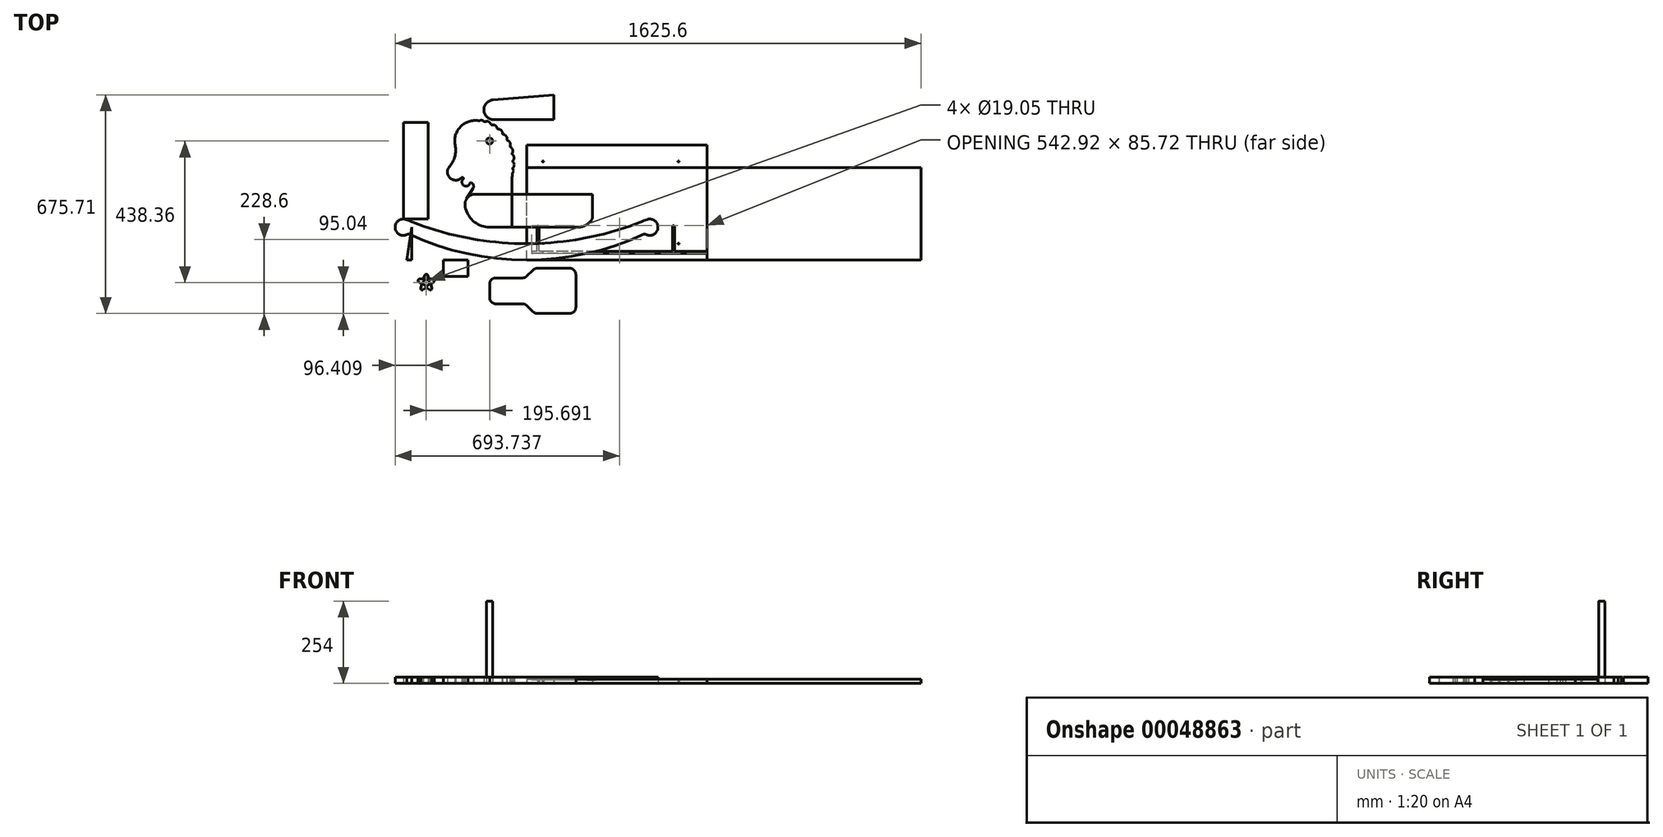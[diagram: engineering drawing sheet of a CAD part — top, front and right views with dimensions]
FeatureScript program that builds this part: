
annotation { "Feature Type Name" : "Feature", "Feature Type Description" : "" }
export const myFeature = defineFeature(function(context is Context, id is Id, definition is map)
    precondition{}
    {
        {
            var Q0;
            Q0=qCreatedBy(makeId("Top.planeOp"),FACE);
            var sketch = newSketch(context, id + "F23", { "sketchPlane" : qUnion([Q0])});
            skArc(sketch, "E0", {"start": v(368.4, 79.55) * mm, "mid": v(406.35, 100.02) * mm, "end": v(371.23, 125.05) * mm});
            skArc(sketch, "E1", {"start": v(-371.23, 125.05) * mm, "mid": v(-406.35, 100.02) * mm, "end": v(-368.4, 79.55) * mm});
            skArc(sketch, "E2", {"start": v(-362.58, 79.8) * mm, "mid": v(0, 0) * mm, "end": v(362.58, 79.8) * mm});
            skArc(sketch, "E3", {"start": v(-371.23, 125.05) * mm, "mid": v(-305.78, 100.52) * mm, "end": v(-238.73, 80.79) * mm});
            skPoint(sketch, "E4.visualSharp", {"position": v(365.76, 81.28) * mm});
            skArc(sketch, "E4.filletArc", {"start": v(368.4, 79.55) * mm, "mid": v(365.52, 80.38) * mm, "end": v(362.58, 79.8) * mm});
            skPoint(sketch, "E5.visualSharp", {"position": v(-365.76, 81.28) * mm});
            skArc(sketch, "E5.filletArc", {"start": v(-362.58, 79.8) * mm, "mid": v(-365.52, 80.38) * mm, "end": v(-368.4, 79.55) * mm});
            skLineSegment(sketch, "E6", {"start": v(-238.73, 80.79) * mm, "end": v(-151.67, 62.8) * mm});
            skArc(sketch, "E7.trimOffspring", {"start": v(-151.67, 62.8) * mm, "mid": v(0, 50.8) * mm, "end": v(151.67, 62.8) * mm});
            skLineSegment(sketch, "E8", {"start": v(238.73, 80.79) * mm, "end": v(151.67, 62.8) * mm});
            skArc(sketch, "E9.trimOffspring", {"start": v(238.73, 80.79) * mm, "mid": v(305.78, 100.52) * mm, "end": v(371.23, 125.05) * mm});
            skSolve(sketch);
        }
        {
            var Q0;
            Q0 = qSketchRegion(id + "F23", true);
            extrude(context, id + "F0", {"entities" : qUnion([Q0]), "depth" : 19.05 * mm});
        }
        {
            var Q0;
            Q0=qCreatedBy(makeId("Top.planeOp"),FACE);
            var sketch = newSketch(context, id + "F1", { "sketchPlane" : qUnion([Q0])});
            skLineSegment(sketch, "E10.bottom", {"start": v(-190.5, 203.2) * mm, "end": v(203.2, 203.2) * mm, "construction": true});
            skLineSegment(sketch, "E10.top", {"start": v(-190.5, 101.6) * mm, "end": v(203.2, 101.6) * mm, "construction": true});
            skLineSegment(sketch, "E10.left", {"start": v(-190.5, 203.2) * mm, "end": v(-190.5, 101.6) * mm, "construction": true});
            skLineSegment(sketch, "E10.right", {"start": v(203.2, 203.2) * mm, "end": v(203.2, 101.6) * mm, "construction": true});
            skArc(sketch, "E11", {"start": v(-165.1, 203.2) * mm, "mid": v(-185.7, 188.88) * mm, "end": v(-189.47, 164.07) * mm});
            skLineSegment(sketch, "E12", {"start": v(-189.47, 164.07) * mm, "end": v(-188.03, 158.55) * mm});
            skArc(sketch, "E13", {"start": v(-188.03, 158.55) * mm, "mid": v(-160.88, 117.5) * mm, "end": v(-114.3, 101.6) * mm});
            skArc(sketch, "E14", {"start": v(159.2, 101.6) * mm, "mid": v(183.79, 107.94) * mm, "end": v(202.23, 125.39) * mm});
            skLineSegment(sketch, "E15", {"start": v(-165.1, 203.2) * mm, "end": v(203.2, 203.2) * mm});
            skLineSegment(sketch, "E16", {"start": v(203.2, 203.2) * mm, "end": v(203.2, 128.76) * mm});
            skLineSegment(sketch, "E17", {"start": v(159.2, 101.6) * mm, "end": v(-114.3, 101.6) * mm});
            skPoint(sketch, "E18.visualSharp", {"position": v(203.2, 127) * mm});
            skArc(sketch, "E18.filletArc", {"start": v(202.23, 125.39) * mm, "mid": v(202.95, 127) * mm, "end": v(203.2, 128.76) * mm});
            skArc(sketch, "E19", {"start": v(-165.57, 221.2) * mm, "mid": v(-164.08, 231.17) * mm, "end": v(-170.33, 239.1) * mm});
            skArc(sketch, "E20", {"start": v(-196.2, 250.12) * mm, "mid": v(-193.66, 230.45) * mm, "end": v(-175.03, 237.24) * mm});
            skArc(sketch, "E21", {"start": v(-238.28, 289.15) * mm, "mid": v(-236.44, 253.68) * mm, "end": v(-200.95, 254.7) * mm});
            skArc(sketch, "E22", {"start": v(-146.05, 430.52) * mm, "mid": v(-203.79, 413.06) * mm, "end": v(-220.89, 355.22) * mm});
            skLineSegment(sketch, "E23", {"start": v(-185.7, 188.88) * mm, "end": v(-165.57, 221.2) * mm});
            skArc(sketch, "E24", {"start": v(-238.28, 289.15) * mm, "mid": v(-221.76, 320.12) * mm, "end": v(-220.89, 355.22) * mm});
            skArc(sketch, "E25", {"start": v(-44.45, 306.08) * mm, "mid": v(-73.08, 386.4) * mm, "end": v(-146.05, 430.52) * mm, "construction": true});
            skLineSegment(sketch, "E26", {"start": v(-44.45, 305.7) * mm, "end": v(-44.45, 203.2) * mm, "construction": true});
            skArc(sketch, "E27", {"start": v(-196.2, 250.12) * mm, "mid": v(-196.28, 254.8) * mm, "end": v(-200.95, 254.7) * mm});
            skLineSegment(sketch, "E28", {"start": v(-220.72, 382.14) * mm, "end": v(-244, 277.9) * mm, "construction": true});
            skLineSegment(sketch, "E29", {"start": v(-44.45, 203.2) * mm, "end": v(-44.45, 101.6) * mm});
            skLineSegment(sketch, "E30", {"start": v(-219.22, 272.35) * mm, "end": v(-187.06, 241.3) * mm, "construction": true});
            skPoint(sketch, "E31.visualSharp", {"position": v(-174.4, 240.46) * mm});
            skArc(sketch, "E31.filletArc", {"start": v(-170.33, 239.1) * mm, "mid": v(-173.11, 239.26) * mm, "end": v(-175.03, 237.24) * mm});
            skArc(sketch, "E32", {"start": v(-130.35, 426.25) * mm, "mid": v(-137.13, 432.31) * mm, "end": v(-146.05, 430.52) * mm});
            skArc(sketch, "E33", {"start": v(-109.75, 417.09) * mm, "mid": v(-117.27, 427.93) * mm, "end": v(-130.35, 426.25) * mm});
            skArc(sketch, "E34", {"start": v(-91.1, 404.43) * mm, "mid": v(-96.58, 416.43) * mm, "end": v(-109.75, 417.09) * mm});
            skArc(sketch, "E35", {"start": v(-74.97, 388.67) * mm, "mid": v(-78.24, 401.45) * mm, "end": v(-91.1, 404.43) * mm});
            skArc(sketch, "E36", {"start": v(-61.89, 370.3) * mm, "mid": v(-62.85, 383.47) * mm, "end": v(-74.97, 388.67) * mm});
            skArc(sketch, "E37", {"start": v(-52.26, 349.92) * mm, "mid": v(-50.88, 363.04) * mm, "end": v(-61.89, 370.3) * mm});
            skArc(sketch, "E38", {"start": v(-46.38, 328.16) * mm, "mid": v(-42.7, 340.83) * mm, "end": v(-52.26, 349.92) * mm});
            skArc(sketch, "E39", {"start": v(-44.45, 305.7) * mm, "mid": v(-38.6, 317.51) * mm, "end": v(-46.38, 328.16) * mm});
            skArc(sketch, "E40", {"start": v(-44.45, 283.7) * mm, "mid": v(-38.1, 294.7) * mm, "end": v(-44.45, 305.7) * mm});
            skArc(sketch, "E41", {"start": v(-44.45, 267.83) * mm, "mid": v(-40.64, 275.77) * mm, "end": v(-44.45, 283.7) * mm});
            skArc(sketch, "E42", {"start": v(-44.45, 259.4) * mm, "mid": v(-43.18, 263.62) * mm, "end": v(-44.45, 267.83) * mm});
            skLineSegment(sketch, "E43", {"start": v(-44.45, 259.4) * mm, "end": v(-44.45, 203.2) * mm});
            skCircle(sketch, "E44", {"center": v(-114.3, 368.3) * mm, "radius": 9.53 * mm});
            skSolve(sketch);
        }
        {
            var Q0;
            Q0=qCreatedBy(makeId("Top.planeOp"),FACE);
            var sketch = newSketch(context, id + "F2", { "sketchPlane" : qUnion([Q0])});
            skLineSegment(sketch, "E45.bottom", {"start": v(-95.25, -55.25) * mm, "end": v(-12.34, -55.25) * mm});
            skLineSegment(sketch, "E45.top", {"start": v(-95.25, -135.26) * mm, "end": v(-12.34, -135.26) * mm});
            skLineSegment(sketch, "E45.left", {"start": v(-114.3, -74.3) * mm, "end": v(-114.3, -116.2) * mm});
            skLineSegment(sketch, "E46.bottom", {"start": v(33.3, -25.4) * mm, "end": v(133.35, -25.4) * mm});
            skLineSegment(sketch, "E46.top", {"start": v(33.3, -165.1) * mm, "end": v(133.35, -165.1) * mm});
            skLineSegment(sketch, "E46.right", {"start": v(152.4, -44.45) * mm, "end": v(152.4, -146.05) * mm});
            skLineSegment(sketch, "E47", {"start": v(1.13, -49.67) * mm, "end": v(19.82, -30.98) * mm});
            skLineSegment(sketch, "E48", {"start": v(1.13, -140.83) * mm, "end": v(19.82, -159.52) * mm});
            skPoint(sketch, "E49.visualSharp", {"position": v(-4.45, -55.25) * mm});
            skArc(sketch, "E49.filletArc", {"start": v(-12.34, -55.25) * mm, "mid": v(-5.05, -53.8) * mm, "end": v(1.13, -49.67) * mm});
            skPoint(sketch, "E50.visualSharp", {"position": v(25.4, -25.4) * mm});
            skArc(sketch, "E50.filletArc", {"start": v(33.3, -25.4) * mm, "mid": v(26, -26.85) * mm, "end": v(19.82, -30.98) * mm});
            skPoint(sketch, "E51.visualSharp", {"position": v(-4.44, -135.26) * mm});
            skArc(sketch, "E51.filletArc", {"start": v(1.13, -140.83) * mm, "mid": v(-5.05, -136.7) * mm, "end": v(-12.34, -135.26) * mm});
            skPoint(sketch, "E52.visualSharp", {"position": v(25.4, -165.1) * mm});
            skArc(sketch, "E52.filletArc", {"start": v(19.82, -159.52) * mm, "mid": v(26, -163.65) * mm, "end": v(33.3, -165.1) * mm});
            skLineSegment(sketch, "E53", {"start": v(-114.3, -95.25) * mm, "end": v(152.4, -95.25) * mm, "construction": true});
            skPoint(sketch, "E54.visualSharp", {"position": v(-114.3, -55.25) * mm});
            skArc(sketch, "E54.filletArc", {"start": v(-95.25, -55.24) * mm, "mid": v(-108.72, -60.82) * mm, "end": v(-114.3, -74.3) * mm});
            skPoint(sketch, "E55.visualSharp", {"position": v(-114.3, -135.25) * mm});
            skArc(sketch, "E55.filletArc", {"start": v(-114.3, -116.2) * mm, "mid": v(-108.72, -129.68) * mm, "end": v(-95.25, -135.26) * mm});
            skPoint(sketch, "E56.visualSharp", {"position": v(152.4, -165.1) * mm});
            skArc(sketch, "E56.filletArc", {"start": v(133.35, -165.1) * mm, "mid": v(146.82, -159.52) * mm, "end": v(152.4, -146.05) * mm});
            skPoint(sketch, "E57.visualSharp", {"position": v(152.4, -25.4) * mm});
            skArc(sketch, "E57.filletArc", {"start": v(152.4, -44.45) * mm, "mid": v(146.82, -30.98) * mm, "end": v(133.35, -25.4) * mm});
            skSolve(sketch);
        }
        {
            var Q0;
            Q0=qCreatedBy(makeId("Top.planeOp"),FACE);
            var sketch = newSketch(context, id + "F3", { "sketchPlane" : qUnion([Q0])});
            skLineSegment(sketch, "E58.bottom", {"start": v(-381, 425.45) * mm, "end": v(-304.8, 425.45) * mm});
            skLineSegment(sketch, "E58.top", {"start": v(-381, 127) * mm, "end": v(-304.8, 127) * mm});
            skLineSegment(sketch, "E58.left", {"start": v(-381, 425.45) * mm, "end": v(-381, 127) * mm});
            skLineSegment(sketch, "E58.right", {"start": v(-304.8, 425.45) * mm, "end": v(-304.8, 127) * mm});
            skSolve(sketch);
        }
        {
            var Q0;
            Q0=qCreatedBy(makeId("Top.planeOp"),FACE);
            var sketch = newSketch(context, id + "F4", { "sketchPlane" : qUnion([Q0])});
            skLineSegment(sketch, "E59", {"start": v(-370.84, 0) * mm, "end": v(-355.6, 101.6) * mm});
            skLineSegment(sketch, "E60", {"start": v(-355.6, 101.6) * mm, "end": v(-355.6, 0) * mm});
            skLineSegment(sketch, "E61", {"start": v(-355.6, 0) * mm, "end": v(-370.84, 0) * mm});
            skCircle(sketch, "E62.cCircle", {"center": v(-310, -70.06) * mm, "radius": 37.8 * mm, "construction": true});
            skLineSegment(sketch, "E62.0", {"start": v(-332.21, -100.64) * mm, "end": v(-345.95, -58.38) * mm, "construction": true});
            skLineSegment(sketch, "E62.1", {"start": v(-345.95, -58.38) * mm, "end": v(-310, -32.25) * mm, "construction": true});
            skLineSegment(sketch, "E62.2", {"start": v(-310, -32.25) * mm, "end": v(-274.04, -58.38) * mm, "construction": true});
            skLineSegment(sketch, "E62.3", {"start": v(-274.04, -58.38) * mm, "end": v(-287.77, -100.64) * mm, "construction": true});
            skLineSegment(sketch, "E62.4", {"start": v(-287.77, -100.64) * mm, "end": v(-332.21, -100.64) * mm, "construction": true});
            skLineSegment(sketch, "E63", {"start": v(-330.31, -58.38) * mm, "end": v(-320.88, -58.38) * mm});
            skLineSegment(sketch, "E64", {"start": v(-319.56, -91.45) * mm, "end": v(-311.93, -85.91) * mm});
            skLineSegment(sketch, "E65", {"start": v(-300.42, -91.45) * mm, "end": v(-308.05, -85.91) * mm});
            skLineSegment(sketch, "E66", {"start": v(-314.82, -47.12) * mm, "end": v(-317.74, -56.1) * mm});
            skLineSegment(sketch, "E67", {"start": v(-305.16, -47.12) * mm, "end": v(-302.24, -56.1) * mm});
            skLineSegment(sketch, "E68.trimOffspring", {"start": v(-295.52, -76.8) * mm, "end": v(-292.6, -85.78) * mm});
            skLineSegment(sketch, "E69.trimOffspring", {"start": v(-299.1, -58.38) * mm, "end": v(-289.67, -58.38) * mm});
            skLineSegment(sketch, "E70.trimOffspring", {"start": v(-324.47, -76.8) * mm, "end": v(-327.38, -85.78) * mm});
            skLineSegment(sketch, "E71.trimOffspring", {"start": v(-325.67, -73.11) * mm, "end": v(-333.3, -67.57) * mm});
            skLineSegment(sketch, "E72.trimOffspring", {"start": v(-294.32, -73.11) * mm, "end": v(-286.69, -67.57) * mm});
            skPoint(sketch, "E73.visualSharp", {"position": v(-301.5, -58.38) * mm});
            skArc(sketch, "E73.filletArc", {"start": v(-302.24, -56.1) * mm, "mid": v(-301.05, -57.75) * mm, "end": v(-299.1, -58.38) * mm});
            skPoint(sketch, "E74.visualSharp", {"position": v(-318.48, -58.38) * mm});
            skArc(sketch, "E74.filletArc", {"start": v(-320.88, -58.38) * mm, "mid": v(-318.94, -57.75) * mm, "end": v(-317.74, -56.1) * mm});
            skPoint(sketch, "E75.visualSharp", {"position": v(-323.72, -74.52) * mm});
            skArc(sketch, "E75.filletArc", {"start": v(-324.47, -76.8) * mm, "mid": v(-324.47, -74.76) * mm, "end": v(-325.67, -73.11) * mm});
            skPoint(sketch, "E76.visualSharp", {"position": v(-310, -84.5) * mm});
            skArc(sketch, "E76.filletArc", {"start": v(-308.05, -85.91) * mm, "mid": v(-310, -85.28) * mm, "end": v(-311.93, -85.91) * mm});
            skPoint(sketch, "E77.visualSharp", {"position": v(-296.26, -74.52) * mm});
            skArc(sketch, "E77.filletArc", {"start": v(-294.32, -73.11) * mm, "mid": v(-295.52, -74.76) * mm, "end": v(-295.52, -76.8) * mm});
            skCircle(sketch, "E78", {"center": v(-310, -70.06) * mm, "radius": 9.53 * mm});
            skPoint(sketch, "E79.visualSharp", {"position": v(-310, -32.25) * mm});
            skArc(sketch, "E79.filletArc", {"start": v(-305.16, -47.12) * mm, "mid": v(-310, -43.61) * mm, "end": v(-314.82, -47.12) * mm});
            skPoint(sketch, "E80.visualSharp", {"position": v(-274.04, -58.38) * mm});
            skArc(sketch, "E80.filletArc", {"start": v(-286.69, -67.57) * mm, "mid": v(-284.84, -61.89) * mm, "end": v(-289.67, -58.38) * mm});
            skPoint(sketch, "E81.visualSharp", {"position": v(-345.95, -58.38) * mm});
            skArc(sketch, "E81.filletArc", {"start": v(-330.31, -58.38) * mm, "mid": v(-335.14, -61.89) * mm, "end": v(-333.3, -67.57) * mm});
            skPoint(sketch, "E82.visualSharp", {"position": v(-332.21, -100.64) * mm});
            skArc(sketch, "E82.filletArc", {"start": v(-327.38, -85.78) * mm, "mid": v(-325.54, -91.45) * mm, "end": v(-319.56, -91.45) * mm});
            skPoint(sketch, "E83.visualSharp", {"position": v(-287.77, -100.64) * mm});
            skArc(sketch, "E83.filletArc", {"start": v(-300.42, -91.45) * mm, "mid": v(-294.45, -91.45) * mm, "end": v(-292.6, -85.78) * mm});
            skSolve(sketch);
        }
        {
            var Q0;
            Q0=qCreatedBy(makeId("Top.planeOp"),FACE);
            var sketch = newSketch(context, id + "F5", { "sketchPlane" : qUnion([Q0])});
            skLineSegment(sketch, "E84.bottom", {"start": v(83.86, 510.61) * mm, "end": v(-104.04, 495.27) * mm});
            skLineSegment(sketch, "E84.top", {"start": v(83.86, 434.41) * mm, "end": v(-101.56, 434.41) * mm});
            skLineSegment(sketch, "E84.left", {"start": v(83.86, 510.61) * mm, "end": v(83.86, 434.41) * mm});
            skArc(sketch, "E85", {"start": v(-104.04, 495.27) * mm, "mid": v(-132.02, 463.65) * mm, "end": v(-101.56, 434.41) * mm});
            skSolve(sketch);
        }
        {
            var Q0;
            Q0=makeQuery(id+"F3.imprint","IMPRINT",FACE,{"disambiguationData":[TD([[makeQuery(id+"F3.imprint","IMPRINT",EDGE,{"derivedFrom":sQuery(id+"F3.wireOp",EDGE,"E58.bottom")}),-1.0]])]});
            extrude(context, id + "F6", {"entities" : qUnion([Q0]), "depth" : 19.05 * mm});
        }
        {
            var Q0;
            Q0=makeQuery(id+"F1.imprint","IMPRINT",FACE,{"disambiguationData":[TD([[makeQuery(id+"F1.imprint","IMPRINT",EDGE,{"derivedFrom":sQuery(id+"F1.wireOp",EDGE,"E11")}),1.0]])]});
            var Q1;
            {var subQ1=sQuery(id+"F1.wireOp",EDGE,"E14");Q1=makeQuery(id+"F1.imprint","IMPRINT",FACE,{"disambiguationData":[TD([[makeQuery(id+"F1.imprint","IMPRINT",EDGE,{"derivedFrom":subQ1}),1.0]])]});}
            extrude(context, id + "F7", {"entities" : qUnion([Q0, Q1]), "depth" : 19.05 * mm});
        }
        {
            var Q0;
            Q0=makeQuery(id+"F4.imprint","IMPRINT",FACE,{"disambiguationData":[TD([[makeQuery(id+"F4.imprint","IMPRINT",EDGE,{"derivedFrom":sQuery(id+"F4.wireOp",EDGE,"E59")}),-1.0]])]});
            extrude(context, id + "F8", {"entities" : qUnion([Q0]), "depth" : 19.05 * mm});
        }
        {
            var Q0;
            Q0=makeQuery(id+"F2.imprint","IMPRINT",FACE,{"disambiguationData":[TD([[makeQuery(id+"F2.imprint","IMPRINT",EDGE,{"derivedFrom":sQuery(id+"F2.wireOp",EDGE,"E45.bottom")}),-1.0]])]});
            extrude(context, id + "F24", {"entities" : qUnion([Q0]), "depth" : 19.05 * mm});
        }
        {
            var Q0;
            Q0=makeQuery(id+"F5.imprint","IMPRINT",FACE,{"disambiguationData":[TD([[makeQuery(id+"F5.imprint","IMPRINT",EDGE,{"derivedFrom":sQuery(id+"F5.wireOp",EDGE,"E84.bottom")}),1.0]])]});
            extrude(context, id + "F9", {"entities" : qUnion([Q0]), "depth" : 19.05 * mm});
        }
        {
            var Q0;
            {var subQ1=sQuery(id+"F1.wireOp",EDGE,"E12");Q0=makeQuery(id+"F1.imprint","IMPRINT",FACE,{"disambiguationData":[TD([[makeQuery(id+"F1.imprint","IMPRINT",EDGE,{"derivedFrom":subQ1}),1.0]])]});}
            var Q1;
            Q1=makeQuery(id+"F1.imprint","IMPRINT",FACE,{"disambiguationData":[TD([[makeQuery(id+"F1.imprint","IMPRINT",EDGE,{"derivedFrom":sQuery(id+"F1.wireOp",EDGE,"E19")}),-1.0]])]});
            extrude(context, id + "F10", {"entities" : qUnion([Q0, Q1]), "depth" : 19.05 * mm});
        }
        {
            var Q0;
            Q0=makeQuery(id+"F4.imprint","IMPRINT",FACE,{"disambiguationData":[TD([[makeQuery(id+"F4.imprint","IMPRINT",EDGE,{"derivedFrom":sQuery(id+"F4.wireOp",EDGE,"E63")}),-1.0]])]});
            extrude(context, id + "F11", {"entities" : qUnion([Q0]), "depth" : 19.05 * mm});
        }
        {
            var Q0;
            Q0=qCreatedBy(makeId("Top.planeOp"),FACE);
            var sketch = newSketch(context, id + "F12", { "sketchPlane" : qUnion([Q0])});
            skLineSegment(sketch, "E86.bottom", {"start": v(0, 0) * mm, "end": v(1219.2, 0) * mm});
            skLineSegment(sketch, "E86.top", {"start": v(0, 285.75) * mm, "end": v(1219.2, 285.75) * mm});
            skLineSegment(sketch, "E86.left", {"start": v(0, 0) * mm, "end": v(0, 285.75) * mm});
            skLineSegment(sketch, "E86.right", {"start": v(1219.2, 0) * mm, "end": v(1219.2, 285.75) * mm});
            skSolve(sketch);
        }
        {
            var Q0;
            Q0=makeQuery(id+"F12.imprint","IMPRINT",FACE,{"disambiguationData":[TD([[makeQuery(id+"F12.imprint","IMPRINT",EDGE,{"derivedFrom":sQuery(id+"F12.wireOp",EDGE,"E86.bottom")}),1.0]])]});
            extrude(context, id + "F13", {"entities" : qUnion([Q0]), "depth" : 12.7 * mm});
        }
        {
            var Q0;
            Q0=qCreatedBy(makeId("Top.planeOp"),FACE);
            var sketch = newSketch(context, id + "F14", { "sketchPlane" : qUnion([Q0])});
            skLineSegment(sketch, "E87.bottom", {"start": v(-256.73, 0) * mm, "end": v(-180.53, 0) * mm});
            skLineSegment(sketch, "E87.top", {"start": v(-256.73, -50.8) * mm, "end": v(-180.53, -50.8) * mm});
            skLineSegment(sketch, "E87.left", {"start": v(-256.73, 0) * mm, "end": v(-256.73, -50.8) * mm});
            skLineSegment(sketch, "E87.right", {"start": v(-180.53, 0) * mm, "end": v(-180.53, -50.8) * mm});
            skSolve(sketch);
        }
        {
            var Q0;
            Q0=makeQuery(id+"F14.imprint","IMPRINT",FACE,{"disambiguationData":[TD([[makeQuery(id+"F14.imprint","IMPRINT",EDGE,{"derivedFrom":sQuery(id+"F14.wireOp",EDGE,"E87.bottom")}),-1.0]])]});
            extrude(context, id + "F15", {"entities" : qUnion([Q0]), "depth" : 19.05 * mm});
        }
        {
            var Q0;
            Q0=qCreatedBy(makeId("Top.planeOp"),FACE);
            var sketch = newSketch(context, id + "F16", { "sketchPlane" : qUnion([Q0])});
            skLineSegment(sketch, "E88.bottom", {"start": v(0, 0) * mm, "end": v(558.8, 0) * mm});
            skLineSegment(sketch, "E88.top", {"start": v(0, 355.6) * mm, "end": v(558.8, 355.6) * mm});
            skLineSegment(sketch, "E88.left", {"start": v(0, 0) * mm, "end": v(0, 355.6) * mm});
            skLineSegment(sketch, "E88.right", {"start": v(558.8, 0) * mm, "end": v(558.8, 355.6) * mm});
            skPoint(sketch, "E89", {"position": v(50.8, 304.8) * mm});
            skPoint(sketch, "E90", {"position": v(50.8, 50.8) * mm});
            skPoint(sketch, "E91", {"position": v(469.9, 304.8) * mm});
            skPoint(sketch, "E92", {"position": v(469.9, 50.8) * mm});
            skLineSegment(sketch, "E93", {"start": v(50.8, 304.8) * mm, "end": v(50.8, 50.8) * mm, "construction": true});
            skLineSegment(sketch, "E94", {"start": v(50.8, 304.8) * mm, "end": v(469.9, 304.8) * mm, "construction": true});
            skLineSegment(sketch, "E95", {"start": v(469.9, 50.8) * mm, "end": v(469.9, 304.8) * mm, "construction": true});
            skLineSegment(sketch, "E96", {"start": v(469.9, 50.8) * mm, "end": v(50.8, 50.8) * mm, "construction": true});
            skCircle(sketch, "E97", {"center": v(50.8, 304.8) * mm, "radius": 1.59 * mm});
            skCircle(sketch, "E98", {"center": v(469.9, 304.8) * mm, "radius": 1.59 * mm});
            skCircle(sketch, "E99", {"center": v(469.9, 50.8) * mm, "radius": 1.59 * mm});
            skCircle(sketch, "E100", {"center": v(50.8, 50.8) * mm, "radius": 1.59 * mm});
            skLineSegment(sketch, "E101", {"start": v(50.8, 50.8) * mm, "end": v(50.8, 25.4) * mm, "construction": true});
            skLineSegment(sketch, "E102", {"start": v(469.9, 25.4) * mm, "end": v(469.9, 50.8) * mm, "construction": true});
            skLineSegment(sketch, "E103", {"start": v(50.8, 25.4) * mm, "end": v(469.9, 25.4) * mm, "construction": true});
            skCircle(sketch, "E104", {"center": v(50.8, 25.4) * mm, "radius": 1.59 * mm});
            skCircle(sketch, "E105", {"center": v(469.9, 25.4) * mm, "radius": 1.59 * mm});
            skCircle(sketch, "E106", {"center": v(36.51, 50.8) * mm, "radius": 1.59 * mm});
            skLineSegment(sketch, "E107", {"start": v(50.8, 50.8) * mm, "end": v(36.51, 50.8) * mm, "construction": true});
            skSolve(sketch);
        }
        {
            var Q0;
            Q0=makeQuery(id+"F16.imprint","IMPRINT",FACE,{"disambiguationData":[TD([[makeQuery(id+"F16.imprint","IMPRINT",EDGE,{"derivedFrom":sQuery(id+"F16.wireOp",EDGE,"E88.bottom")}),1.0]])]});
            extrude(context, id + "F17", {"entities" : qUnion([Q0]), "depth" : 12.7 * mm});
        }
        {
            var Q0;
            Q0=makeQuery(id+"F10.opExtrude","SWEPT_EDGE",EDGE,{"disambiguationData":[OSD([sQuery(id+"F1.wireOp",EDGE,"E22"),sQuery(id+"F1.wireOp",EDGE,"E32")])]});
            var Q1;
            Q1=makeQuery(id+"F10.opExtrude","SWEPT_EDGE",EDGE,{"disambiguationData":[OSD([sQuery(id+"F1.wireOp",EDGE,"E32"),sQuery(id+"F1.wireOp",EDGE,"E33")])]});
            var Q2;
            Q2=makeQuery(id+"F10.opExtrude","SWEPT_EDGE",EDGE,{"disambiguationData":[OSD([sQuery(id+"F1.wireOp",EDGE,"E33"),sQuery(id+"F1.wireOp",EDGE,"E34")])]});
            var Q3;
            Q3=makeQuery(id+"F10.opExtrude","SWEPT_EDGE",EDGE,{"disambiguationData":[OSD([sQuery(id+"F1.wireOp",EDGE,"E34"),sQuery(id+"F1.wireOp",EDGE,"E35")])]});
            var Q4;
            Q4=makeQuery(id+"F10.opExtrude","SWEPT_EDGE",EDGE,{"disambiguationData":[OSD([sQuery(id+"F1.wireOp",EDGE,"E35"),sQuery(id+"F1.wireOp",EDGE,"E36")])]});
            var Q5;
            Q5=makeQuery(id+"F10.opExtrude","SWEPT_EDGE",EDGE,{"disambiguationData":[OSD([sQuery(id+"F1.wireOp",EDGE,"E36"),sQuery(id+"F1.wireOp",EDGE,"E37")])]});
            var Q6;
            Q6=makeQuery(id+"F10.opExtrude","SWEPT_EDGE",EDGE,{"disambiguationData":[OSD([sQuery(id+"F1.wireOp",EDGE,"E37"),sQuery(id+"F1.wireOp",EDGE,"E38")])]});
            var Q7;
            Q7=makeQuery(id+"F10.opExtrude","SWEPT_EDGE",EDGE,{"disambiguationData":[OSD([sQuery(id+"F1.wireOp",EDGE,"E38"),sQuery(id+"F1.wireOp",EDGE,"E39")])]});
            var Q8;
            Q8=makeQuery(id+"F10.opExtrude","SWEPT_EDGE",EDGE,{"disambiguationData":[OSD([sQuery(id+"F1.wireOp",EDGE,"E39"),sQuery(id+"F1.wireOp",EDGE,"E40")])]});
            var Q9;
            Q9=makeQuery(id+"F10.opExtrude","SWEPT_EDGE",EDGE,{"disambiguationData":[OSD([sQuery(id+"F1.wireOp",EDGE,"E40"),sQuery(id+"F1.wireOp",EDGE,"E41")])]});
            var Q10;
            Q10=makeQuery(id+"F10.opExtrude","SWEPT_EDGE",EDGE,{"disambiguationData":[OSD([sQuery(id+"F1.wireOp",EDGE,"E41"),sQuery(id+"F1.wireOp",EDGE,"E42")])]});
            var Q11;
            Q11=makeQuery(id+"F10.opExtrude","SWEPT_EDGE",EDGE,{"disambiguationData":[OSD([sQuery(id+"F1.wireOp",EDGE,"E42"),sQuery(id+"F1.wireOp",EDGE,"E43")])]});
            fillet(context, id + "F18", {"entities" : qUnion([Q0, Q1, Q2, Q3, Q4, Q5, Q6, Q7, Q8, Q9, Q10, Q11]), "radius" : 3.3 * mm, "tangentPropagation" : true, "allowEdgeOverflow" : false});
        }
        {
            var Q0;
            Q0=makeQuery(id+"F1.imprint","IMPRINT",FACE,{"disambiguationData":[TD([[makeQuery(id+"F1.imprint","IMPRINT",EDGE,{"derivedFrom":sQuery(id+"F1.wireOp",EDGE,"E44")}),1.0]])]});
            extrude(context, id + "F19", {"entities" : qUnion([Q0]), "depth" : 254 * mm});
        }
        {
            var Q0;
            Q0=makeQuery(id+"F0.opExtrude","SWEPT_EDGE",EDGE,{"disambiguationData":[OSD([sQuery(id+"F23.wireOp",EDGE,"E3"),sQuery(id+"F23.wireOp",EDGE,"E6")])]});
            var Q1;
            Q1=makeQuery(id+"F0.opExtrude","SWEPT_EDGE",EDGE,{"disambiguationData":[OSD([sQuery(id+"F23.wireOp",EDGE,"E6"),sQuery(id+"F23.wireOp",EDGE,"E7.trimOffspring")])]});
            var Q2;
            Q2=makeQuery(id+"F0.opExtrude","SWEPT_EDGE",EDGE,{"disambiguationData":[OSD([sQuery(id+"F23.wireOp",EDGE,"E7.trimOffspring"),sQuery(id+"F23.wireOp",EDGE,"E8")])]});
            var Q3;
            Q3=makeQuery(id+"F0.opExtrude","SWEPT_EDGE",EDGE,{"disambiguationData":[OSD([sQuery(id+"F23.wireOp",EDGE,"E8"),sQuery(id+"F23.wireOp",EDGE,"E9.trimOffspring")])]});
            fillet(context, id + "F20", {"entities" : qUnion([Q0, Q1, Q2, Q3]), "radius" : 5.08 * mm, "tangentPropagation" : true, "allowEdgeOverflow" : false});
        }
        {
            var Q0;
            Q0=makeQuery(id+"F17.opExtrude","CAP_FACE",FACE,{"disambiguationData":[OSD([sQuery(id+"F16.wireOp",EDGE,"E88.bottom"),sQuery(id+"F16.wireOp",EDGE,"E88.top"),sQuery(id+"F16.wireOp",EDGE,"E88.left"),sQuery(id+"F16.wireOp",EDGE,"E88.right"),sQuery(id+"F16.wireOp",EDGE,"E97"),sQuery(id+"F16.wireOp",EDGE,"E98"),sQuery(id+"F16.wireOp",EDGE,"E99"),sQuery(id+"F16.wireOp",EDGE,"E100"),sQuery(id+"F16.wireOp",EDGE,"E104"),sQuery(id+"F16.wireOp",EDGE,"E105"),sQuery(id+"F16.wireOp",EDGE,"E106")])],"isStart":false});
            var sketch = newSketch(context, id + "F21", { "sketchPlane" : qUnion([Q0])});
            skLineSegment(sketch, "E108.bottom", {"start": v(558.8, 26.99) * mm, "end": v(457.2, 26.99) * mm});
            skLineSegment(sketch, "E108.top", {"start": v(558.8, 20.64) * mm, "end": v(19.05, 20.64) * mm});
            skLineSegment(sketch, "E108.left", {"start": v(558.8, 26.99) * mm, "end": v(558.8, 20.64) * mm});
            skLineSegment(sketch, "E109.left", {"start": v(38.1, 26.99) * mm, "end": v(38.1, 103.19) * mm});
            skLineSegment(sketch, "E109.right", {"start": v(31.75, 26.99) * mm, "end": v(31.75, 103.19) * mm});
            skArc(sketch, "E110", {"start": v(38.1, 103.19) * mm, "mid": v(34.93, 106.36) * mm, "end": v(31.75, 103.19) * mm});
            skLineSegment(sketch, "E111.trimOffspring", {"start": v(31.75, 26.99) * mm, "end": v(19.05, 26.99) * mm});
            skArc(sketch, "E112", {"start": v(19.05, 26.99) * mm, "mid": v(15.88, 23.81) * mm, "end": v(19.05, 20.64) * mm});
            skCircle(sketch, "E113", {"center": v(454.03, 103.19) * mm, "radius": 3.18 * mm});
            skLineSegment(sketch, "E114", {"start": v(450.85, 103.19) * mm, "end": v(450.85, 26.99) * mm});
            skLineSegment(sketch, "E115", {"start": v(457.2, 103.19) * mm, "end": v(457.2, 26.99) * mm});
            skLineSegment(sketch, "E116.trimOffspring", {"start": v(450.85, 26.99) * mm, "end": v(38.1, 26.99) * mm});
            skSolve(sketch);
        }
        {
            var Q0;
            Q0 = qSketchRegion(id + "F21", true);
            extrude(context, id + "F22", {"entities" : qUnion([Q0]), "operationType" : NewBodyOperationType.REMOVE, "oppositeDirection" : true, "depth" : 3.17 * mm});
        }
    });
